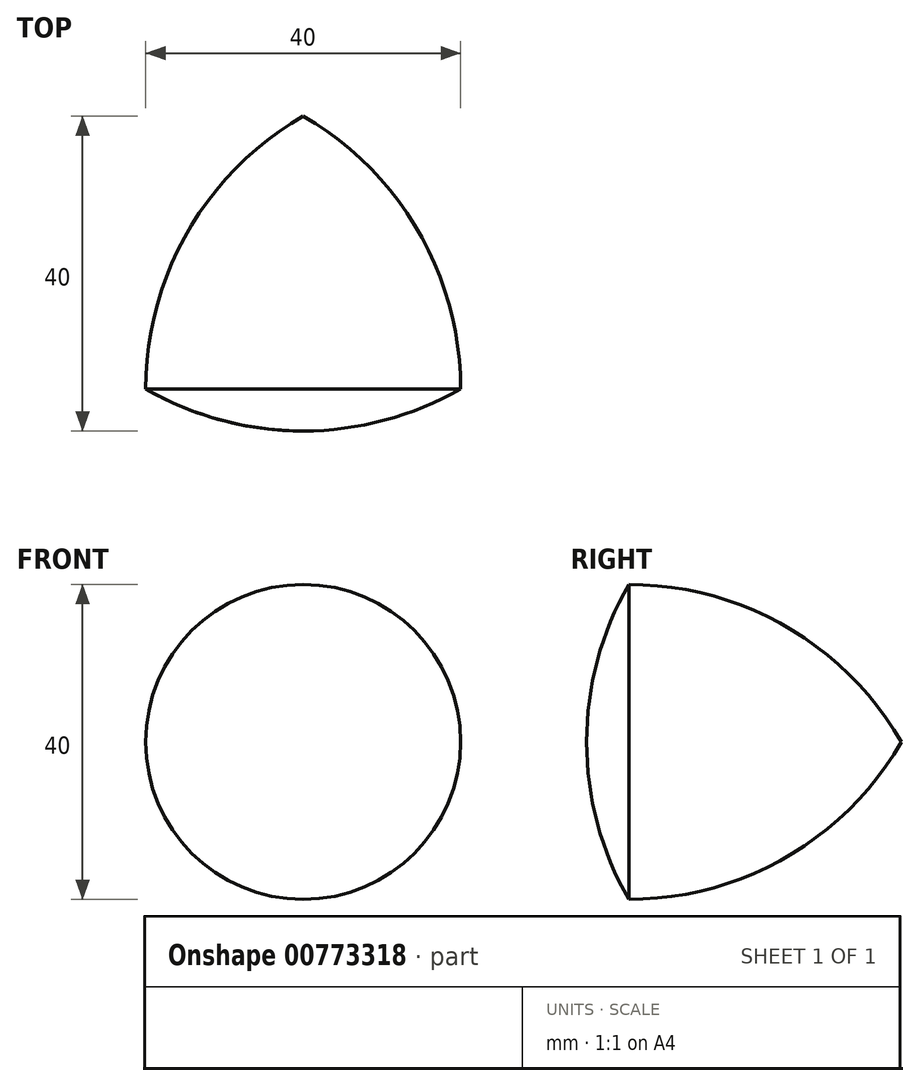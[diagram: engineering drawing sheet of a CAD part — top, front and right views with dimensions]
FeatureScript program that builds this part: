
annotation { "Feature Type Name" : "Feature", "Feature Type Description" : "" }
export const myFeature = defineFeature(function(context is Context, id is Id, definition is map)
    precondition{}
    {
        {
            var Q0;
            Q0=qCreatedBy(makeId("Top.planeOp"),FACE);
            var sketch = newSketch(context, id + "F0", { "sketchPlane" : qUnion([Q0])});
            skLineSegment(sketch, "E0", {"start": v(-20, -11.55) * mm, "end": v(0, 23.1) * mm, "construction": true});
            skLineSegment(sketch, "E1", {"start": v(0, 23.1) * mm, "end": v(20, -11.55) * mm, "construction": true});
            skLineSegment(sketch, "E2", {"start": v(20, -11.55) * mm, "end": v(-20, -11.55) * mm, "construction": true});
            skLineSegment(sketch, "E3", {"start": v(0, 23.1) * mm, "end": v(0, 0) * mm, "construction": true});
            skLineSegment(sketch, "E4", {"start": v(0, 0) * mm, "end": v(20, -11.55) * mm, "construction": true});
            skLineSegment(sketch, "E5", {"start": v(0, 0) * mm, "end": v(-20, -11.55) * mm, "construction": true});
            skCircle(sketch, "E6", {"center": v(-20, -11.55) * mm, "radius": 40 * mm});
            skCircle(sketch, "E7", {"center": v(20, -11.55) * mm, "radius": 40 * mm});
            skCircle(sketch, "E8", {"center": v(0, 23.1) * mm, "radius": 40 * mm});
            skLineSegment(sketch, "E9", {"start": v(0, 23.1) * mm, "end": v(0, -16.9) * mm});
            skSolve(sketch);
        }
        {
            var Q0;
            {var subQ0=sQuery(id+"F0.wireOp",EDGE,"E9");Q0=makeQuery(id+"F0.imprint","IMPRINT",FACE,{"disambiguationData":[TD([[makeQuery(id+"F0.imprint","IMPRINT",EDGE,{"derivedFrom":subQ0}),-1.0]])]});}
            var Q1;
            Q1=sQuery(id+"F0.wireOp",EDGE,"E9");
            revolve(context, id + "F1", {"surfaceOperationType" : NewSurfaceOperationType.NEW, "entities" : qUnion([Q0]), "axis" : qUnion([Q1]), "revolveType" : RevolveType.FULL});
        }
    });
